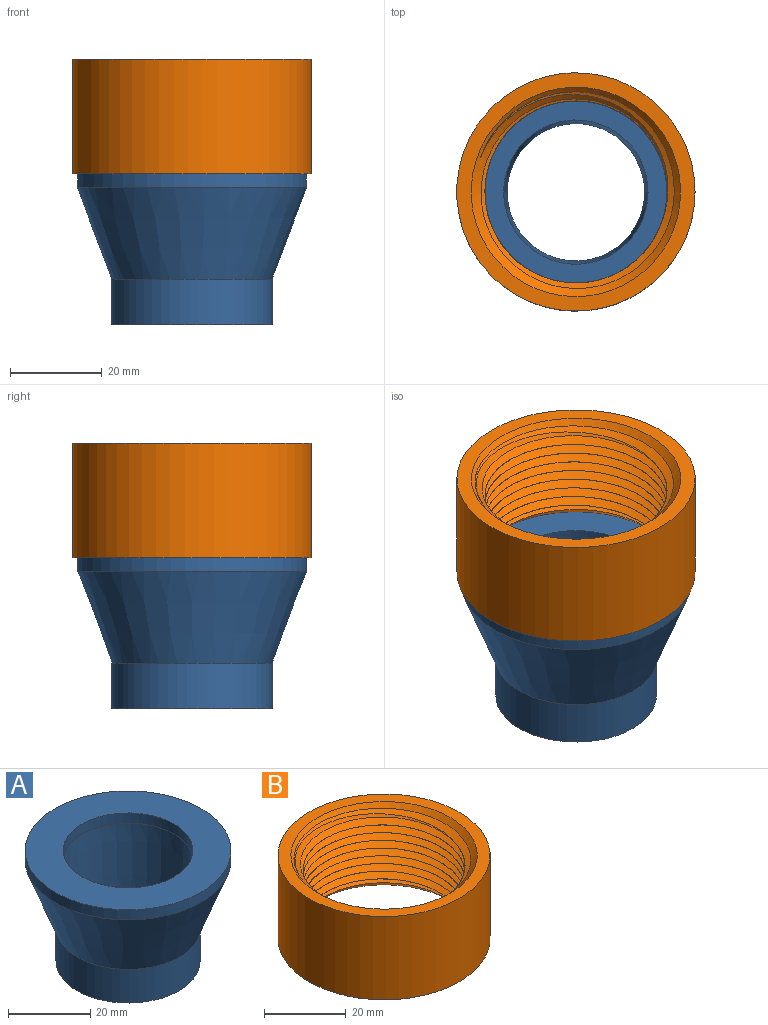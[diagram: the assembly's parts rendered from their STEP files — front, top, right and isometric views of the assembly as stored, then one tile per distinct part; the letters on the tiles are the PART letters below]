
ASSEMBLY  parts=2 mates=1
PART A: 8 faces, bbox 50x50x33 mm
  f0: plane 50x50mm, normal (0,0,1), area 1184.2mm2, adj f1,f7
  f1: cylinder r=15.75mm len=31.5mm, axis (0,0,1), area 296.9mm2, adj f0,f2
  f2: cone r=15.75mm half-angle=2.1deg, axis (0,0,1), area 1933.4mm2, adj f1,f3
  f3: cylinder r=15mm len=30mm, axis (0,0,1), area 942.5mm2, adj f2,f4
  f4: plane 35x35mm, normal (0,0,-1), area 255.3mm2, adj f3,f5
  f5: cylinder r=17.5mm len=35mm, axis (0,0,1), area 1099.6mm2, adj f4,f6
  f6: cone r=17.5mm half-angle=20.6deg, axis (0,0,1), area 2851.9mm2, adj f5,f7
  f7: cylinder r=25mm len=50mm, axis (0,0,1), area 471.2mm2, adj f0,f6
PART B: 10 faces, bbox 52x52x26.2 mm
  f0: cylinder r=19.85mm len=39.7mm, axis (0,0,-1), area 36.5mm2, adj f4,f7,f8,f9
  f1: cylinder r=26mm len=52mm, axis (0,0,-1), area 4084.1mm2, adj f2,f3
  f2: plane 52x52mm, normal (0,0,1), area 483.4mm2, adj f1,f6
  f3: plane 52x52mm, normal (0,0,-1), area 483.4mm2, adj f1,f5
  f4: cone r=22.85mm half-angle=45deg, axis (0,0,-1), area 0mm2, adj f0,f5,f8
  f5: cone r=22.85mm half-angle=45deg, axis (0,0,-1), area 359.8mm2, adj f3,f4,f8,f9
  f6: cone r=19.85mm half-angle=45deg, axis (0,0,1), area 358.9mm2, adj f2,f7,f8,f9
  f7: cone r=19.85mm half-angle=45deg, axis (0,0,1), area 0.9mm2, adj f0,f6,f8,f9
  f8: bspline ~50.38x48.07mm, area 3114.7mm2, adj f0,f4,f5,f6,f7,f9
  f9: bspline ~50.38x48.07mm, area 3128.7mm2, adj f0,f5,f6,f7,f8
PLACE A at identity
PLACE B t=(0,0,33)mm
MATE fastened B.f1 <-> A.f1  axis (0,0,-1) through (0,0,33)mm
